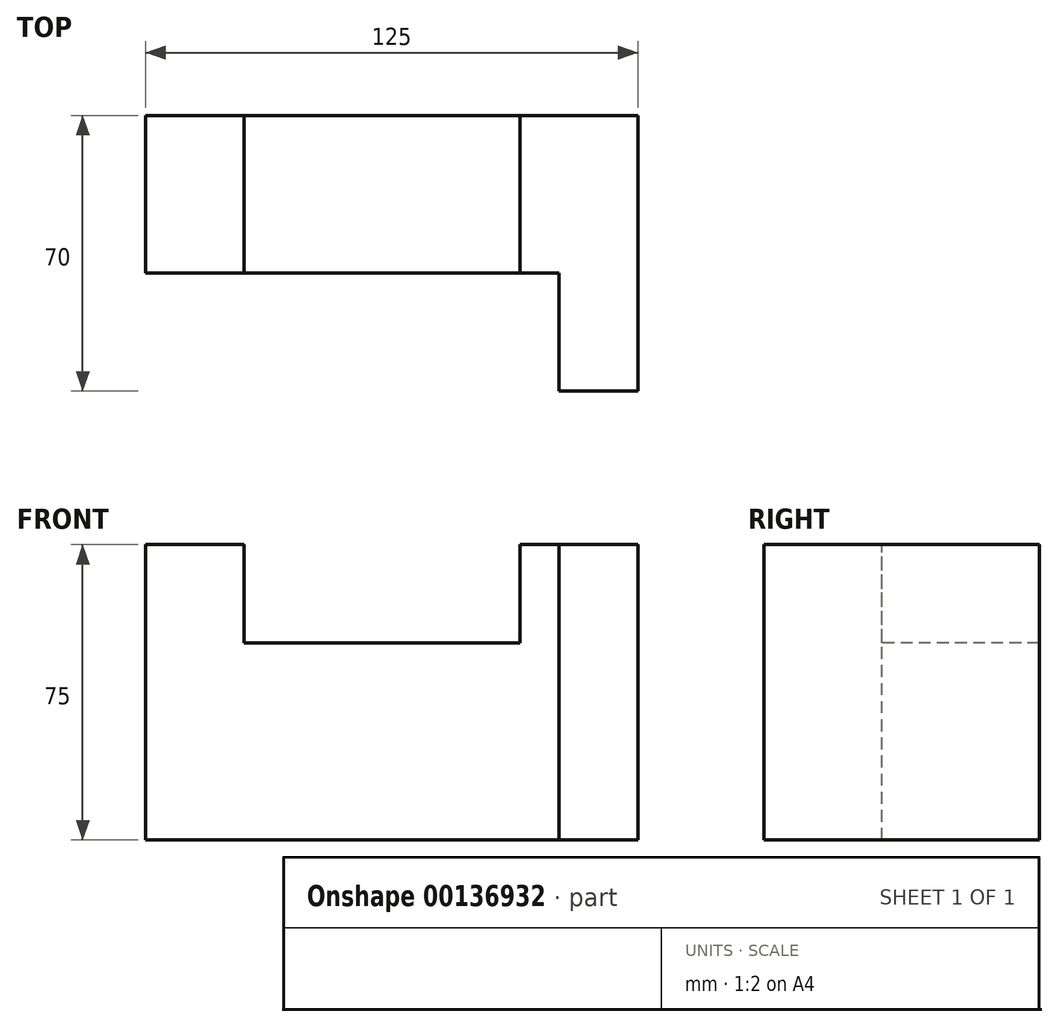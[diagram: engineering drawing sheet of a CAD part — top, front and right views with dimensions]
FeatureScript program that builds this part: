
annotation { "Feature Type Name" : "Feature", "Feature Type Description" : "" }
export const myFeature = defineFeature(function(context is Context, id is Id, definition is map)
    precondition{}
    {
        {
            var Q0;
            Q0=qCreatedBy(makeId("Front.planeOp"),FACE);
            var sketch = newSketch(context, id + "F0", { "sketchPlane" : qUnion([Q0])});
            skLineSegment(sketch, "E0.bottom", {"start": v(0, 0) * mm, "end": v(125, 0) * mm});
            skLineSegment(sketch, "E0.top", {"start": v(0, 75) * mm, "end": v(125, 75) * mm});
            skLineSegment(sketch, "E0.left", {"start": v(0, 0) * mm, "end": v(0, 75) * mm});
            skLineSegment(sketch, "E0.right", {"start": v(125, 0) * mm, "end": v(125, 75) * mm});
            skSolve(sketch);
        }
        {
            var Q0;
            Q0=makeQuery(id+"F0.imprint","IMPRINT",FACE,{"disambiguationData":[TD([[makeQuery(id+"F0.imprint","IMPRINT",EDGE,{"derivedFrom":sQuery(id+"F0.wireOp",EDGE,"E0.bottom")}),1.0]])]});
            extrude(context, id + "F1", {"entities" : qUnion([Q0]), "endBound" : BoundingType.SYMMETRIC, "depth" : 70 * mm});
        }
        {
            var Q0;
            Q0=makeQuery(id+"F1.opExtrude","CAP_FACE",FACE,{"disambiguationData":[OSD([sQuery(id+"F0.wireOp",EDGE,"E0.bottom"),sQuery(id+"F0.wireOp",EDGE,"E0.top"),sQuery(id+"F0.wireOp",EDGE,"E0.left"),sQuery(id+"F0.wireOp",EDGE,"E0.right")])],"isStart":false});
            var sketch = newSketch(context, id + "F2", { "sketchPlane" : qUnion([Q0])});
            skLineSegment(sketch, "E1.bottom", {"start": v(25, 75) * mm, "end": v(95, 75) * mm});
            skLineSegment(sketch, "E1.top", {"start": v(25, 50) * mm, "end": v(95, 50) * mm});
            skLineSegment(sketch, "E1.left", {"start": v(25, 75) * mm, "end": v(25, 50) * mm});
            skLineSegment(sketch, "E1.right", {"start": v(95, 75) * mm, "end": v(95, 50) * mm});
            skSolve(sketch);
        }
        {
            var Q0;
            Q0=makeQuery(id+"F2.imprint","IMPRINT",FACE,{"disambiguationData":[TD([[makeQuery(id+"F2.imprint","IMPRINT",EDGE,{"derivedFrom":sQuery(id+"F2.wireOp",EDGE,"E1.bottom")}),-1.0]])]});
            extrude(context, id + "F3", {"entities" : qUnion([Q0]), "operationType" : NewBodyOperationType.REMOVE, "endBound" : BoundingType.THROUGH_ALL, "oppositeDirection" : true, "depth" : 25 * mm});
        }
        {
            var Q0;
            {var subQ0=sQuery(id+"F0.wireOp",EDGE,"E0.right");var subQ2=sQuery(id+"F0.wireOp",EDGE,"E0.top");Q0=makeQuery(id+"F3.boolean.opBoolean","SPLIT",FACE,{"disambiguationData":[TD([makeQuery(id+"F1.opExtrude","SWEPT_FACE",FACE,{"disambiguationData":[OSD([subQ0])]})])],"derivedFrom":makeQuery(id+"F1.opExtrude","SWEPT_FACE",FACE,{"disambiguationData":[OSD([subQ2])]})});}
            var sketch = newSketch(context, id + "F4", { "sketchPlane" : qUnion([Q0])});
            skLineSegment(sketch, "E2.bottom", {"start": v(0, -35) * mm, "end": v(105, -35) * mm});
            skLineSegment(sketch, "E2.top", {"start": v(0, -5) * mm, "end": v(105, -5) * mm});
            skLineSegment(sketch, "E2.left", {"start": v(0, -35) * mm, "end": v(0, -5) * mm});
            skLineSegment(sketch, "E2.right", {"start": v(105, -35) * mm, "end": v(105, -5) * mm});
            skLineSegment(sketch, "E3.bottom", {"start": v(42.5, -5) * mm, "end": v(70, -5) * mm});
            skLineSegment(sketch, "E3.top", {"start": v(42.5, 10) * mm, "end": v(70, 10) * mm});
            skLineSegment(sketch, "E3.left", {"start": v(42.5, -5) * mm, "end": v(42.5, 10) * mm});
            skLineSegment(sketch, "E3.right", {"start": v(70, -5) * mm, "end": v(70, 10) * mm});
            skSolve(sketch);
        }
        {
            var Q0;
            {var subQ0=sQuery(id+"F4.wireOp",EDGE,"E2.left");Q0=makeQuery(id+"F4.imprint","IMPRINT",FACE,{"disambiguationData":[TD([[makeQuery(id+"F4.imprint","IMPRINT",EDGE,{"derivedFrom":subQ0}),-1.0]])]});}
            var Q1;
            Q1=makeQuery(id+"F4.imprint","IMPRINT",FACE,{"disambiguationData":[TD([[makeQuery(id+"F4.imprint","IMPRINT",EDGE,{"derivedFrom":sQuery(id+"F4.wireOp",EDGE,"E3.bottom")}),1.0]])]});
            var Q2;
            {var subQ5=sQuery(id+"F4.wireOp",EDGE,"E2.right");Q2=makeQuery(id+"F4.imprint","IMPRINT",FACE,{"disambiguationData":[TD([[makeQuery(id+"F4.imprint","IMPRINT",EDGE,{"derivedFrom":subQ5}),1.0]])]});}
            extrude(context, id + "F5", {"entities" : qUnion([Q0, Q1, Q2]), "operationType" : NewBodyOperationType.REMOVE, "endBound" : BoundingType.THROUGH_ALL, "oppositeDirection" : true, "depth" : 25 * mm});
        }
    });
